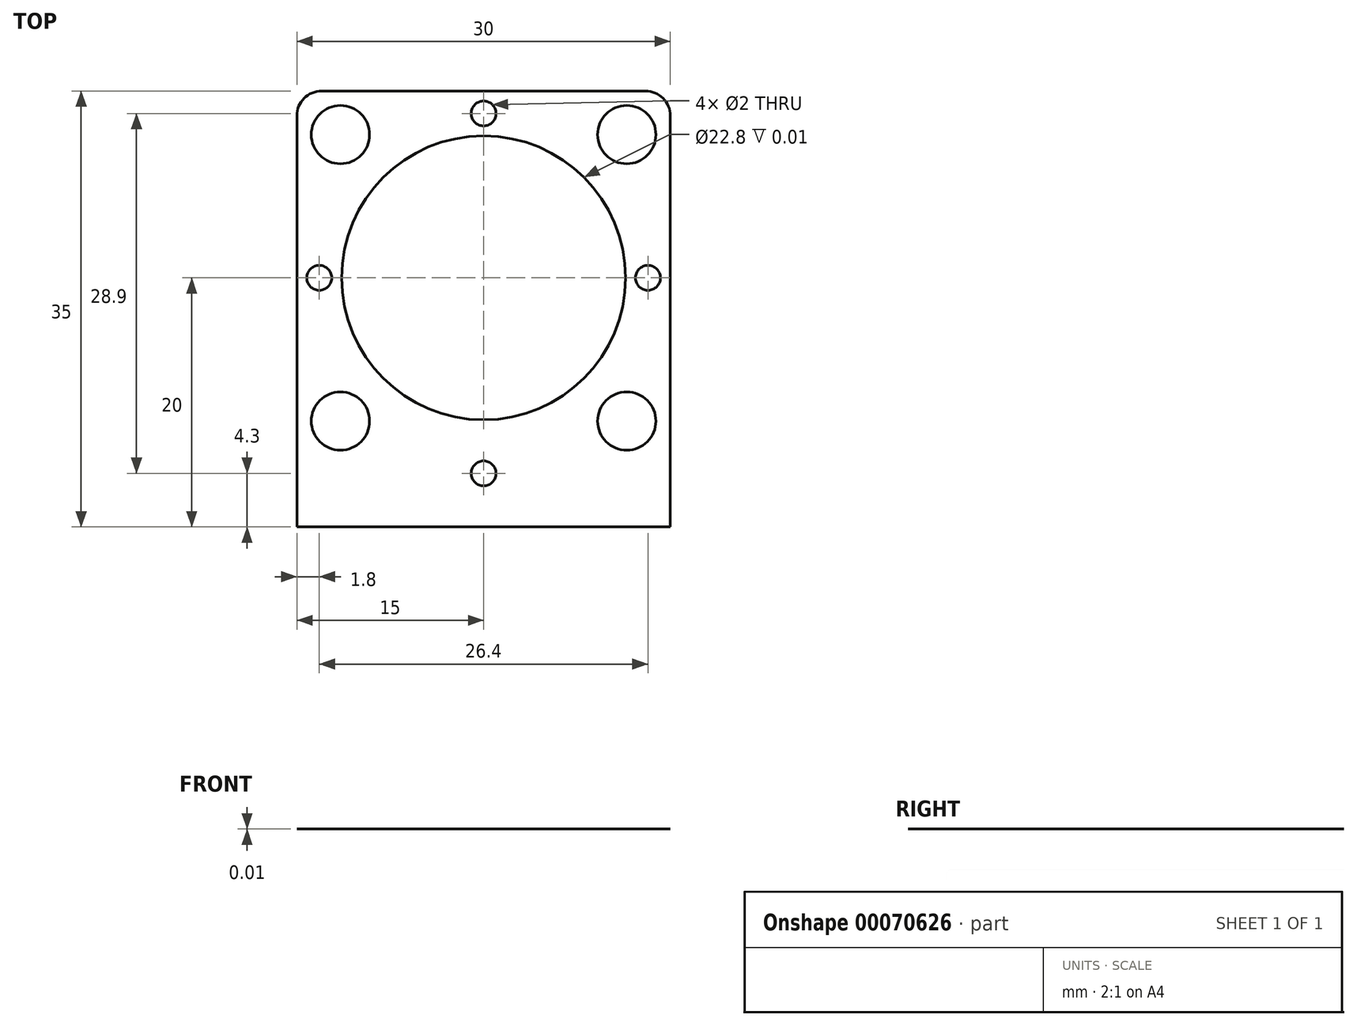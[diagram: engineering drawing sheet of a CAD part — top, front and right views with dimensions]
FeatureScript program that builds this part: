
annotation { "Feature Type Name" : "Feature", "Feature Type Description" : "" }
export const myFeature = defineFeature(function(context is Context, id is Id, definition is map)
    precondition{}
    {
        {
            var Q0;
            Q0=qCreatedBy(makeId("Top.planeOp"),FACE);
            var sketch = newSketch(context, id + "F0", { "sketchPlane" : qUnion([Q0])});
            skCircle(sketch, "E0", {"center": v(0, 0) * mm, "radius": 11.4 * mm});
            skLineSegment(sketch, "E1", {"start": v(0, 0) * mm, "end": v(0, 12.13) * mm});
            skLineSegment(sketch, "E2.direction1", {"start": v(-11.5, 11.5) * mm, "end": v(11.5, 11.5) * mm, "construction": true});
            skLineSegment(sketch, "E3.bottom", {"start": v(-15, 15) * mm, "end": v(15, 15) * mm});
            skLineSegment(sketch, "E3.top", {"start": v(-15, -20) * mm, "end": v(15, -20) * mm});
            skLineSegment(sketch, "E3.left", {"start": v(-15, 15) * mm, "end": v(-15, -20) * mm});
            skLineSegment(sketch, "E3.right", {"start": v(15, 15) * mm, "end": v(15, -20) * mm});
            skLineSegment(sketch, "E4.bottom", {"start": v(-7.5, -20) * mm, "end": v(7.5, -20) * mm});
            skLineSegment(sketch, "E4.top", {"start": v(-7.5, -26.35) * mm, "end": v(7.5, -26.35) * mm});
            skLineSegment(sketch, "E4.left", {"start": v(-7.5, -20) * mm, "end": v(-7.5, -26.35) * mm});
            skLineSegment(sketch, "E4.right", {"start": v(7.5, -20) * mm, "end": v(7.5, -26.35) * mm});
            skLineSegment(sketch, "E5.MirrorCS", {"start": v(-11.5, -11.5) * mm, "end": v(11.5, -11.5) * mm, "construction": true});
            skPoint(sketch, "E6", {"position": v(0, -23.18) * mm});
            skPoint(sketch, "E7", {"position": v(13.2, 0) * mm});
            skPoint(sketch, "E8.1.0", {"position": v(0, 13.2) * mm});
            skPoint(sketch, "E8.2.0", {"position": v(-13.2, 0) * mm});
            skPoint(sketch, "E8.3.0", {"position": v(0, -15.7) * mm});
            skPoint(sketch, "E9.positionSnap0", {"position": v(0, -11.5) * mm});
            skSolve(sketch);
        }
        {
            var Q0;
            Q0=makeQuery(id+"F0.imprint","IMPRINT",FACE,{"disambiguationData":[TD([[makeQuery(id+"F0.imprint","IMPRINT",EDGE,{"derivedFrom":sQuery(id+"F0.wireOp",EDGE,"E0")}),-1.0]])]});
            var Q1;
            Q1=makeQuery(id+"F0.imprint","IMPRINT",FACE,{"disambiguationData":[TD([[makeQuery(id+"F0.imprint","IMPRINT",EDGE,{"derivedFrom":sQuery(id+"F0.wireOp",EDGE,"E4.bottom")}),-1.0]])]});
            extrude(context, id + "F1", {"entities" : qUnion([Q0, Q1]), "depth" : 1 / 101.6 * mm});
        }
        {
            var Q0;
            Q0=makeQuery(id+"F1.opExtrude","SWEPT_EDGE",EDGE,{"disambiguationData":[OSD([sQuery(id+"F0.wireOp",EDGE,"E3.bottom"),sQuery(id+"F0.wireOp",EDGE,"E3.right")])]});
            var Q1;
            Q1=makeQuery(id+"F1.opExtrude","SWEPT_EDGE",EDGE,{"disambiguationData":[OSD([sQuery(id+"F0.wireOp",EDGE,"E3.bottom"),sQuery(id+"F0.wireOp",EDGE,"E3.left")])]});
            fillet(context, id + "F2", {"entities" : qUnion([Q0, Q1]), "radius" : 2 * mm, "tangentPropagation" : true, "allowEdgeOverflow" : false});
        }
        {
            var Q0;
            {var subQ0=sQuery(id+"F0.wireOp",EDGE,"E3.top");Q0=makeQuery(id+"F1.opExtrude","SWEPT_FACE",FACE,{"disambiguationData":[OSD([subQ0]),TDD([makeQuery(id+"F0.imprint","IMPRINT",EDGE,{"disambiguationData":[TD([[makeQuery(id+"F0.imprint","INTERSECT",VERTEX,{"derivedFrom":[subQ0,sQuery(id+"F0.wireOp",EDGE,"E3.right")]}),1.0]])],"derivedFrom":subQ0})])]});}
            var sketch = newSketch(context, id + "F3", { "sketchPlane" : qUnion([Q0])});
            skPoint(sketch, "E10", {"position": v(11.25, 3.18) * mm});
            skSolve(sketch);
        }
        {
            var Q0;
            {var subQ0=sQuery(id+"F0.wireOp",EDGE,"E3.top");Q0=makeQuery(id+"F1.opExtrude","SWEPT_FACE",FACE,{"disambiguationData":[OSD([subQ0]),TDD([makeQuery(id+"F0.imprint","IMPRINT",EDGE,{"disambiguationData":[TD([[makeQuery(id+"F0.imprint","INTERSECT",VERTEX,{"derivedFrom":[subQ0,sQuery(id+"F0.wireOp",EDGE,"E3.left")]}),-1.0]])],"derivedFrom":subQ0})])]});}
            var sketch = newSketch(context, id + "F4", { "sketchPlane" : qUnion([Q0])});
            skPoint(sketch, "E11", {"position": v(-11.25, 3.18) * mm});
            skSolve(sketch);
        }
        {
            var Q0;
            Q0=sQuery(id+"F4.wireOp",VERTEX,"E11");
            var Q1;
            Q1=sQuery(id+"F3.wireOp",VERTEX,"E10");
            var Q2;
            Q2=makeQuery(id+"F1.opExtrude","SWEPT_BODY",BODY,{"disambiguationData":[OSD([sQuery(id+"F0.wireOp",EDGE,"E0"),sQuery(id+"F0.wireOp",EDGE,"ad13e253-b4d8-4204-8557-6fc238639051"),sQuery(id+"F0.wireOp",EDGE,"E2.1.0.0"),sQuery(id+"F0.wireOp",EDGE,"e3ba892e-b87d-4f28-b95f-4bf1e75580d00.MirrorC"),sQuery(id+"F0.wireOp",EDGE,"e3ba892e-b87d-4f28-b95f-4bf1e75580d01.MirrorC"),sQuery(id+"F0.wireOp",EDGE,"E3.bottom"),sQuery(id+"F0.wireOp",EDGE,"E3.top"),sQuery(id+"F0.wireOp",EDGE,"E3.left"),sQuery(id+"F0.wireOp",EDGE,"E3.right"),sQuery(id+"F0.wireOp",EDGE,"E4.top"),sQuery(id+"F0.wireOp",EDGE,"E4.left"),sQuery(id+"F0.wireOp",EDGE,"E4.right")])]});
            hole(context, id + "F5", {"style" : HoleStyle.SIMPLE, "endStyle" : HoleEndStyle.BLIND, "holeDiameter" : 2.05 * mm, "holeDepth" : 6 * mm, "locations" : qUnion([Q0, Q1]), "scope" : qUnion([Q2])});
        }
        {
            var Q0;
            Q0=sQuery(id+"F0.wireOp",VERTEX,"E2.direction1.start");
            var Q1;
            Q1=sQuery(id+"F0.wireOp",VERTEX,"E2.direction1.end");
            var Q2;
            Q2=sQuery(id+"F0.wireOp",VERTEX,"E5.MirrorCS.start");
            var Q3;
            Q3=sQuery(id+"F0.wireOp",VERTEX,"E5.MirrorCS.end");
            var Q4;
            Q4=sQuery(id+"F0.wireOp",VERTEX,"E6");
            var Q5;
            Q5=makeQuery(id+"F1.opExtrude","SWEPT_BODY",BODY,{"disambiguationData":[OSD([sQuery(id+"F0.wireOp",EDGE,"E0"),sQuery(id+"F0.wireOp",EDGE,"E3.bottom"),sQuery(id+"F0.wireOp",EDGE,"E3.top"),sQuery(id+"F0.wireOp",EDGE,"E3.left"),sQuery(id+"F0.wireOp",EDGE,"E3.right"),sQuery(id+"F0.wireOp",EDGE,"E4.top"),sQuery(id+"F0.wireOp",EDGE,"E4.left"),sQuery(id+"F0.wireOp",EDGE,"E4.right")])]});
            hole(context, id + "F6", {"style" : HoleStyle.C_SINK, "endStyle" : HoleEndStyle.THROUGH, "oppositeDirection" : true, "holeDiameter" : 2.5 * mm, "cSinkDiameter" : 4.7 * mm, "cSinkAngle" : 90 * degree, "locations" : qUnion([Q0, Q1, Q2, Q3, Q4]), "scope" : qUnion([Q5]), "isTappedThrough" : true});
        }
        {
            var Q0;
            Q0=sQuery(id+"F0.wireOp",VERTEX,"E7");
            var Q1;
            Q1=sQuery(id+"F0.wireOp",VERTEX,"E8.1.0");
            var Q2;
            Q2=sQuery(id+"F0.wireOp",VERTEX,"E8.2.0");
            var Q3;
            Q3=sQuery(id+"F0.wireOp",VERTEX,"E8.3.0");
            var Q4;
            Q4=makeQuery(id+"F1.opExtrude","SWEPT_BODY",BODY,{"disambiguationData":[OSD([sQuery(id+"F0.wireOp",EDGE,"E0"),sQuery(id+"F0.wireOp",EDGE,"E3.bottom"),sQuery(id+"F0.wireOp",EDGE,"E3.top"),sQuery(id+"F0.wireOp",EDGE,"E3.left"),sQuery(id+"F0.wireOp",EDGE,"E3.right"),sQuery(id+"F0.wireOp",EDGE,"E4.top"),sQuery(id+"F0.wireOp",EDGE,"E4.left"),sQuery(id+"F0.wireOp",EDGE,"E4.right")])]});
            hole(context, id + "F7", {"style" : HoleStyle.SIMPLE, "endStyle" : HoleEndStyle.BLIND, "oppositeDirection" : true, "holeDiameter" : 2 * mm, "holeDepth" : 8 * mm, "locations" : qUnion([Q0, Q1, Q2, Q3]), "scope" : qUnion([Q4])});
        }
    });
